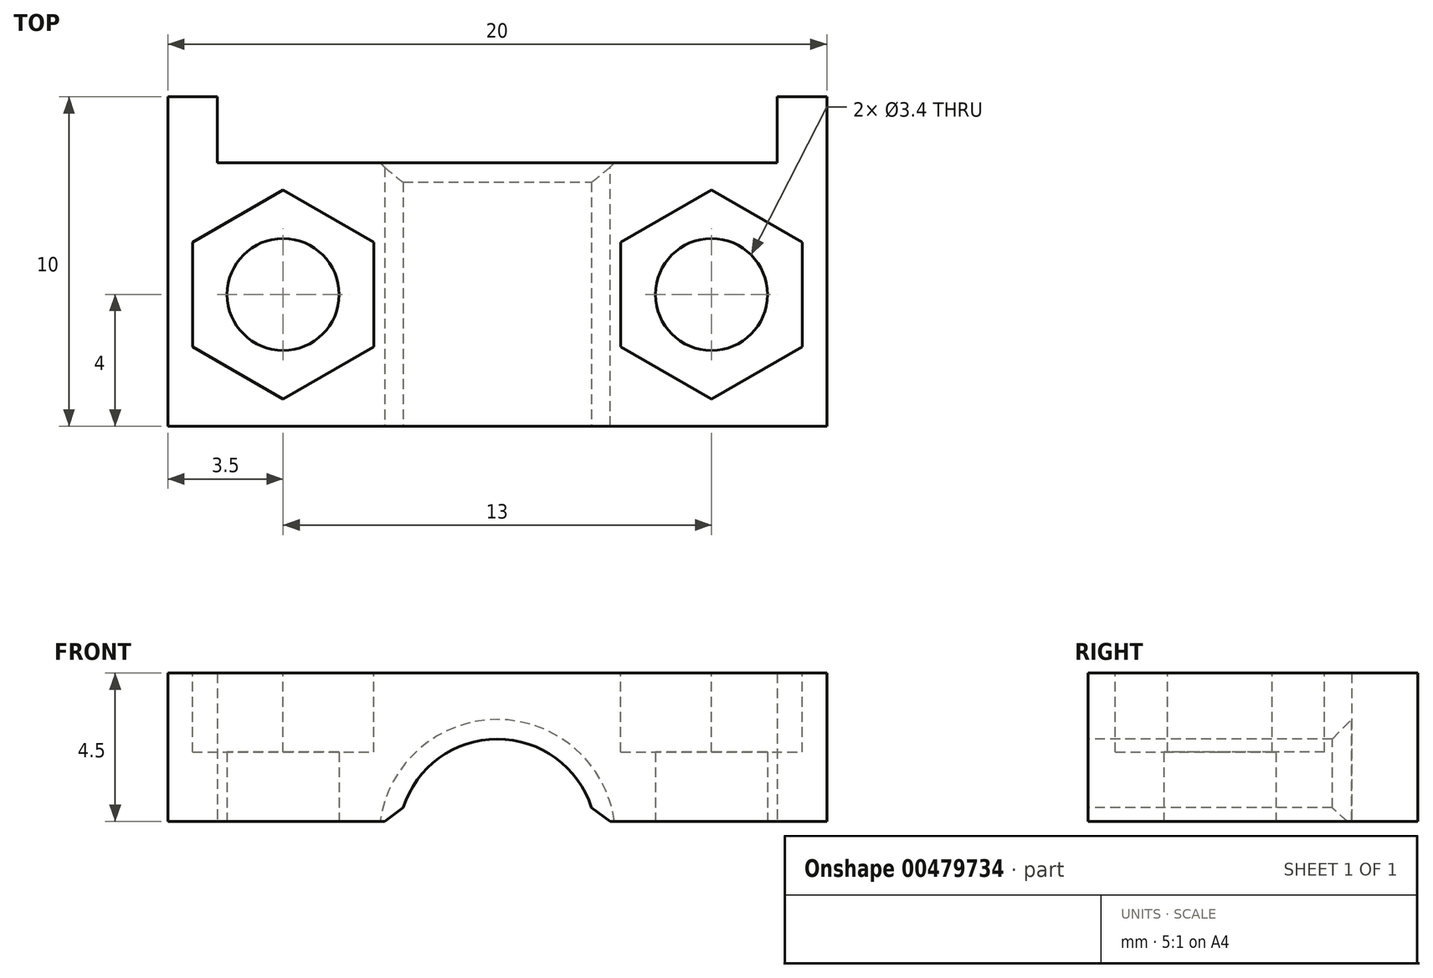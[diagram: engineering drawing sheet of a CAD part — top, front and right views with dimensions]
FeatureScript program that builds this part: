
annotation { "Feature Type Name" : "Feature", "Feature Type Description" : "" }
export const myFeature = defineFeature(function(context is Context, id is Id, definition is map)
    precondition{}
    {
        {
            var Q0;
            Q0=qCreatedBy(makeId("Top.planeOp"),FACE);
            var sketch = newSketch(context, id + "F0", { "sketchPlane" : qUnion([Q0])});
            skLineSegment(sketch, "E0.bottom", {"start": v(0, 0) * mm, "end": v(20, 0) * mm});
            skLineSegment(sketch, "E0.left", {"start": v(0, 0) * mm, "end": v(0, 10) * mm});
            skLineSegment(sketch, "E0.right", {"start": v(20, 0) * mm, "end": v(20, 10) * mm});
            skLineSegment(sketch, "E1", {"start": v(0, 10) * mm, "end": v(1.5, 10) * mm});
            skLineSegment(sketch, "E2", {"start": v(1.5, 10) * mm, "end": v(1.5, 8) * mm});
            skLineSegment(sketch, "E3", {"start": v(1.5, 8) * mm, "end": v(18.5, 8) * mm});
            skLineSegment(sketch, "E4", {"start": v(18.5, 8) * mm, "end": v(18.5, 10) * mm});
            skLineSegment(sketch, "E5", {"start": v(18.5, 10) * mm, "end": v(20, 10) * mm});
            skCircle(sketch, "E6", {"center": v(3.5, 4) * mm, "radius": 1.7 * mm});
            skCircle(sketch, "E7", {"center": v(16.5, 4) * mm, "radius": 1.7 * mm});
            skSolve(sketch);
        }
        {
            var Q0;
            Q0=makeQuery(id+"F0.imprint","IMPRINT",FACE,{"disambiguationData":[TD([[makeQuery(id+"F0.imprint","IMPRINT",EDGE,{"derivedFrom":sQuery(id+"F0.wireOp",EDGE,"E0.bottom")}),1.0]])]});
            extrude(context, id + "F1", {"entities" : qUnion([Q0]), "depth" : 4.5 * mm});
        }
        {
            var Q0;
            Q0=makeQuery(id+"F1.opExtrude","SWEPT_FACE",FACE,{"disambiguationData":[OSD([sQuery(id+"F0.wireOp",EDGE,"E0.bottom")])]});
            var sketch = newSketch(context, id + "F2", { "sketchPlane" : qUnion([Q0])});
            skCircle(sketch, "E8", {"center": v(10, -0.5) * mm, "radius": 3 * mm});
            skSolve(sketch);
        }
        {
            var Q0;
            Q0 = qSketchRegion(id + "F2", true);
            extrude(context, id + "F3", {"entities" : qUnion([Q0]), "operationType" : NewBodyOperationType.REMOVE, "endBound" : BoundingType.THROUGH_ALL, "oppositeDirection" : true, "depth" : 25 * mm});
        }
        {
            var Q0;
            Q0=makeQuery(id+"F1.opExtrude","CAP_FACE",FACE,{"disambiguationData":[OSD([sQuery(id+"F0.wireOp",EDGE,"E0.bottom"),sQuery(id+"F0.wireOp",EDGE,"E0.left"),sQuery(id+"F0.wireOp",EDGE,"E0.right"),sQuery(id+"F0.wireOp",EDGE,"E1"),sQuery(id+"F0.wireOp",EDGE,"E2"),sQuery(id+"F0.wireOp",EDGE,"E3"),sQuery(id+"F0.wireOp",EDGE,"E4"),sQuery(id+"F0.wireOp",EDGE,"E5"),sQuery(id+"F0.wireOp",EDGE,"E6"),sQuery(id+"F0.wireOp",EDGE,"E7")])],"isStart":false});
            var sketch = newSketch(context, id + "F4", { "sketchPlane" : qUnion([Q0])});
            skCircle(sketch, "E9.cCircle", {"center": v(3.5, 4) * mm, "radius": 3.18 * mm, "construction": true});
            skLineSegment(sketch, "E9.0", {"start": v(6.25, 5.59) * mm, "end": v(6.25, 2.41) * mm});
            skLineSegment(sketch, "E9.1", {"start": v(6.25, 2.41) * mm, "end": v(3.5, 0.82) * mm});
            skLineSegment(sketch, "E9.2", {"start": v(3.5, 0.82) * mm, "end": v(0.75, 2.41) * mm});
            skLineSegment(sketch, "E9.3", {"start": v(0.75, 2.41) * mm, "end": v(0.75, 5.59) * mm});
            skLineSegment(sketch, "E9.4", {"start": v(0.75, 5.59) * mm, "end": v(3.5, 7.18) * mm});
            skLineSegment(sketch, "E9.5", {"start": v(3.5, 7.18) * mm, "end": v(6.25, 5.59) * mm});
            skCircle(sketch, "E10.cCircle", {"center": v(16.5, 4) * mm, "radius": 3.18 * mm, "construction": true});
            skLineSegment(sketch, "E10.0", {"start": v(19.25, 5.59) * mm, "end": v(19.25, 2.41) * mm});
            skLineSegment(sketch, "E10.1", {"start": v(19.25, 2.41) * mm, "end": v(16.5, 0.82) * mm});
            skLineSegment(sketch, "E10.2", {"start": v(16.5, 0.82) * mm, "end": v(13.75, 2.41) * mm});
            skLineSegment(sketch, "E10.3", {"start": v(13.75, 2.41) * mm, "end": v(13.75, 5.59) * mm});
            skLineSegment(sketch, "E10.4", {"start": v(13.75, 5.59) * mm, "end": v(16.5, 7.18) * mm});
            skLineSegment(sketch, "E10.5", {"start": v(16.5, 7.18) * mm, "end": v(19.25, 5.59) * mm});
            skSolve(sketch);
        }
        {
            var Q0;
            Q0=makeQuery(id+"F4.imprint","IMPRINT",FACE,{"disambiguationData":[TD([[makeQuery(id+"F4.imprint","IMPRINT",EDGE,{"derivedFrom":sQuery(id+"F4.wireOp",EDGE,"E9.0")}),-1.0]])]});
            var Q1;
            Q1=makeQuery(id+"F4.imprint","IMPRINT",FACE,{"disambiguationData":[TD([[makeQuery(id+"F4.imprint","IMPRINT",EDGE,{"derivedFrom":sQuery(id+"F4.wireOp",EDGE,"E10.0")}),-1.0]])]});
            extrude(context, id + "F5", {"entities" : qUnion([Q0, Q1]), "operationType" : NewBodyOperationType.REMOVE, "oppositeDirection" : true, "depth" : 2.4 * mm});
        }
        {
            var Q0;
            Q0=makeQuery(id+"F3.boolean.opBoolean","INTERSECT",EDGE,{"disambiguationData":[OD(0.0)],"derivedFrom":[makeQuery(id+"F1.opExtrude","CAP_FACE",FACE,{"disambiguationData":[OSD([sQuery(id+"F0.wireOp",EDGE,"E0.bottom"),sQuery(id+"F0.wireOp",EDGE,"E0.left"),sQuery(id+"F0.wireOp",EDGE,"E0.right"),sQuery(id+"F0.wireOp",EDGE,"E1"),sQuery(id+"F0.wireOp",EDGE,"E2"),sQuery(id+"F0.wireOp",EDGE,"E3"),sQuery(id+"F0.wireOp",EDGE,"E4"),sQuery(id+"F0.wireOp",EDGE,"E5"),sQuery(id+"F0.wireOp",EDGE,"E6"),sQuery(id+"F0.wireOp",EDGE,"E7")])],"isStart":true}),makeQuery(id+"F3.opExtrude","SWEPT_FACE",FACE,{"disambiguationData":[OSD([sQuery(id+"F2.wireOp",EDGE,"E8")])]})]});
            var Q1;
            Q1=makeQuery(id+"F3.boolean.opBoolean","INTERSECT",EDGE,{"disambiguationData":[OD(1.0)],"derivedFrom":[makeQuery(id+"F1.opExtrude","CAP_FACE",FACE,{"disambiguationData":[OSD([sQuery(id+"F0.wireOp",EDGE,"E0.bottom"),sQuery(id+"F0.wireOp",EDGE,"E0.left"),sQuery(id+"F0.wireOp",EDGE,"E0.right"),sQuery(id+"F0.wireOp",EDGE,"E1"),sQuery(id+"F0.wireOp",EDGE,"E2"),sQuery(id+"F0.wireOp",EDGE,"E3"),sQuery(id+"F0.wireOp",EDGE,"E4"),sQuery(id+"F0.wireOp",EDGE,"E5"),sQuery(id+"F0.wireOp",EDGE,"E6"),sQuery(id+"F0.wireOp",EDGE,"E7")])],"isStart":true}),makeQuery(id+"F3.opExtrude","SWEPT_FACE",FACE,{"disambiguationData":[OSD([sQuery(id+"F2.wireOp",EDGE,"E8")])]})]});
            var Q2;
            Q2=makeQuery(id+"F3.boolean.opBoolean","INTERSECT",EDGE,{"derivedFrom":[makeQuery(id+"F1.opExtrude","SWEPT_FACE",FACE,{"disambiguationData":[OSD([sQuery(id+"F0.wireOp",EDGE,"E3")])]}),makeQuery(id+"F3.opExtrude","SWEPT_FACE",FACE,{"disambiguationData":[OSD([sQuery(id+"F2.wireOp",EDGE,"E8")])]})]});
            var Q3;
            Q3=makeQuery(id+"F3.boolean.opBoolean","COPY",EDGE,{"derivedFrom":makeQuery(id+"F3.opExtrude","CAP_EDGE",EDGE,{"disambiguationData":[OSD([sQuery(id+"F2.wireOp",EDGE,"E8")])],"isStart":true})});
            chamfer(context, id + "F6", {"entities" : qUnion([Q0, Q1, Q2, Q3]), "chamferType" : ChamferType.TWO_OFFSETS, "width1" : 0.5 * mm, "oppositeDirection" : false, "width2" : 0.5 * mm, "tangentPropagation" : true});
        }
    });
